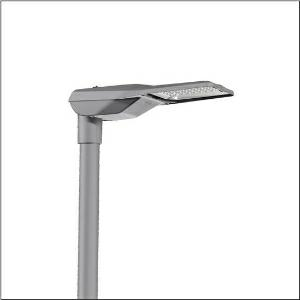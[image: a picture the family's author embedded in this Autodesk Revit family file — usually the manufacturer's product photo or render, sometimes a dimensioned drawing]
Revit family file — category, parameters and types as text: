
# Revit family: streetlight_sl_21_mini___st1_0ab_5xe2m33s08jb_1c43
name_source: partatom
category: Lighting Fixtures
units: mm (PartAtom-declared; Revit-internal decimal feet)

## family parameters
Cut with Voids When Loaded = No
Host = Face
Light Source = No
Part Type = Normal
Room Calculation Point = No
Round Connector Dimension = Use Diameter
Shared = No

## types (1)
- --- (1 x LED, 11390 lm, 88.6 W, 3000K)
    Apparent Load = 89 VA
    CIE Flux Codes = 40 74 97 100 100
    Color Rendering = 70
    Color Temperature = 3000K
    Default Elevation = 1800 mm
    Description = Streetlight SL 21 mini, mast luminaire, primary light control with lens, of PMMA, primary optical cover: cover, of toughened safety glass, transparent, light distribution: ST1.0aB, light emission: direct distribution, primary light characteristic: asymmetric, installation type: side-entry, post-top, LED, High Power LED, rated luminous flux: 11.390lm, luminous efficacy: 129lm/W, light colour: 730, colour temperature: 3000K, control gear: D4i, control: flexible luminous flux parameterisation, time-dependent luminous flux control, constant luminous flux control, overheat protection, pre-setting: logarithmic dimming characteristic, mains connection: 220..240V, AC, 50/60Hz, start of lifetime: 89W, end of service life: 92W, reduction: 41W, luminaire housing, of diecast aluminium, powder-coated, Siteco® metallic grey (DB 702S), corrosivity category C5 mid according to DIN EN ISO 12944, please order mast flange separately, inclination adjustable: 0°, 5°, 10°, 15°, sealing non-destructively replaceable, multi-level sealing system, length: 628mm, width: 235mm, height: 110mm, mast flange for spigot size: 42mm (side-entry): 5XC10008XM4, 60/48mm (side-entry/post-top): 5XC10108XM2, 76/60mm (side-entry/post-top): 5XC10108XM1, mounting height: 4..8m, Smart Interface above, protection rating (complete): IP66, insulation class (complete): insulation class II (safety insulation), certification: CE, ENEC, ENEC+, VDE, impact resistance: IK10, permissible operating ambient temperature for outdoor applications: -40..+50°C, standard-compliant lighting for roads and squares, packaging unit: 1 piece

Light Distribution: ST1.0aB
    Height = 110 mm
    Lamp = 1 x LED
    Lamp Light Flux = 11390 lm
    Lamp Power = 88.6 W
    Lamp count = 1
    Length = 625 mm
    Luminous efficacy = 129 lm/W
    Manufacturer = Siteco
    ModVariant = No
    Model = 5XE2M33S08JB
    Number of Poles = 1
    OnlyDefault = Yes
    Power Factor = 1
    Product Name = Streetlight SL 21 mini | ST1.0aB
    Product group = mast luminaire | pylon top
    ProductGroupID = 6100
    Protection Class = Protection class II
    Protection Degree = IP 66
    RLX_Detail_Level = 1
    RLX_Emergency_Light_Flux = 0 lm
    RLX_Emergency_Type = 0
    RLX_Emergency_Type_DB = No
    RlxData = <blob elided: 26161 chars, md5=0243934c>
    Socket = socket
    Standby Power = 0 W
    System Light Flux = 11390 lm
    System Power = 89 W
    Type Comments = factory setting: luminous flux: 100 % | dim-lin: 254 | 915 mA
    Type Image = l_1003515.jpg
    URL = http://relux.com
    VarID = @adj_030755
    Voltage = 0 V
    Weight = 0.00 kg
    Width = 234 mm

## geometry (parser evidence)
native form markers: Blend x4, Sweep x12
no freeform markers — native parametric forms only
